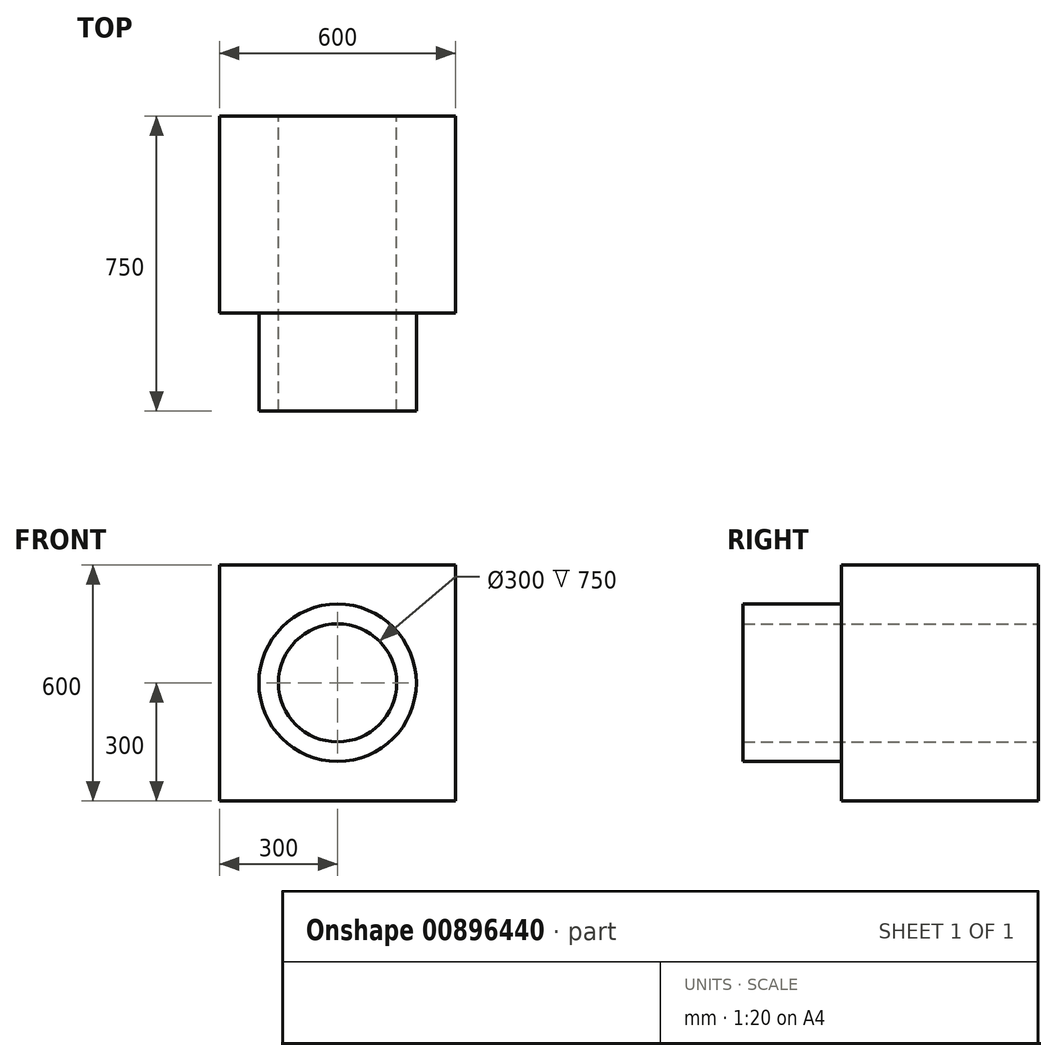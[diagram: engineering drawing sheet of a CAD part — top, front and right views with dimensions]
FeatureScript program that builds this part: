
annotation { "Feature Type Name" : "Feature", "Feature Type Description" : "" }
export const myFeature = defineFeature(function(context is Context, id is Id, definition is map)
    precondition{}
    {
        {
            var Q0;
            Q0=qCreatedBy(makeId("Front.planeOp"),FACE);
            var sketch = newSketch(context, id + "F0", { "sketchPlane" : qUnion([Q0])});
            skLineSegment(sketch, "E0.bottom", {"start": v(-300, 300) * mm, "end": v(300, 300) * mm});
            skLineSegment(sketch, "E0.top", {"start": v(-300, -300) * mm, "end": v(300, -300) * mm});
            skLineSegment(sketch, "E0.left", {"start": v(-300, 300) * mm, "end": v(-300, -300) * mm});
            skLineSegment(sketch, "E0.right", {"start": v(300, 300) * mm, "end": v(300, -300) * mm});
            skSolve(sketch);
        }
        {
            var Q0;
            Q0=makeQuery(id+"F0.imprint","IMPRINT",FACE,{"disambiguationData":[TD([[makeQuery(id+"F0.imprint","IMPRINT",EDGE,{"derivedFrom":sQuery(id+"F0.wireOp",EDGE,"E0.bottom")}),-1.0]])]});
            var Q1;
            Q1 = qSketchRegion(id + "F0", true);
            extrude(context, id + "F1", {"entities" : qUnion([Q0, Q1]), "endBound" : BoundingType.SYMMETRIC, "oppositeDirection" : true, "depth" : 500 * mm, "offsetDistance" : 25.4 * mm});
        }
        {
            var Q0;
            Q0=makeQuery(id+"F1.opExtrude","CAP_FACE",FACE,{"disambiguationData":[OSD([sQuery(id+"F0.wireOp",EDGE,"E0.bottom"),sQuery(id+"F0.wireOp",EDGE,"E0.top"),sQuery(id+"F0.wireOp",EDGE,"E0.left"),sQuery(id+"F0.wireOp",EDGE,"E0.right")])],"isStart":true});
            var sketch = newSketch(context, id + "F2", { "sketchPlane" : qUnion([Q0])});
            skCircle(sketch, "E1", {"center": v(0, 0) * mm, "radius": 200 * mm});
            skCircle(sketch, "E2", {"center": v(0, 0) * mm, "radius": 150 * mm});
            skSolve(sketch);
        }
        {
            var Q0;
            Q0 = qSketchRegion(id + "F2", true);
            extrude(context, id + "F3", {"entities" : qUnion([Q0]), "operationType" : NewBodyOperationType.ADD, "depth" : 250 * mm, "offsetDistance" : 25.4 * mm});
        }
        {
            var Q0;
            Q0=makeQuery(id+"F3.opExtrude","CAP_FACE",FACE,{"disambiguationData":[OSD([sQuery(id+"F2.wireOp",EDGE,"E1"),sQuery(id+"F2.wireOp",EDGE,"E2")])],"isStart":false});
            var sketch = newSketch(context, id + "F4", { "sketchPlane" : qUnion([Q0])});
            skCircle(sketch, "E3", {"center": v(0, 0) * mm, "radius": 150 * mm});
            skSolve(sketch);
        }
        {
            var Q0;
            Q0 = qSketchRegion(id + "F4", true);
            extrude(context, id + "F5", {"entities" : qUnion([Q0]), "operationType" : NewBodyOperationType.REMOVE, "oppositeDirection" : true, "depth" : 1016 * mm, "offsetDistance" : 25.4 * mm});
        }
    });
